# Revit family: BI-12FB
name_source: partatom
category: Устройства связи
units: mm (PartAtom-declared; Revit-internal decimal feet)

## family parameters
Всегда вертикально = Нет
На основе рабочей плоскости = Да
Общий = Да
При загрузке вырезать с полостями = Нет
Размер круглого соединителя = Использовать диаметр
Сохранять ориентацию аннотаций = Нет
Тип детали = Нормальный
Точка принадлежности помещению = Нет

## types (1)
- BI-12FB
    ADSK_URL документации изделия = https://wiki.bas-ip.com
    ADSK_URL страницы изделия = https://www.bas-ip.ru
    ADSK_Версия Revit = Revit 2020
    ADSK_Единица измерения = шт
    ADSK_Завод-изготовитель = BAS-IP
    ADSK_Классификация нагрузок = Вызывная панель
    ADSK_Количество фаз = 1
    ADSK_Коэффициент мощности = 0.9
    ADSK_Марка = BI-12FB
    ADSK_Наименование = ВЫЗЫВНАЯ ПАНЕЛЬ BI-12FB
    ADSK_Наименование краткое = BI-12FB
    ADSK_Напряжение = 12 В
    ADSK_Номинальная мощность = 7 Вт
    ADSK_Полная мощность = 7 В·А
    ADSK_Размер_Длина = 379 мм
    ADSK_Размер_Толщина = 49 мм
    ADSK_Размер_Ширина = 158 мм
    BIM library = https://bimlib.ru
    URL = https://www.bas-ip.ru
    Аутентификация = Отдельный пароль на настройки, WEB–интерфейс
    Выходное видео = HD (1920×1080), H.264 Main Profile
    Группа модели = Вызывная панель
    Дисплей = Нет
    Дополнительно = SIP P2P, Встроенное реле, датчик приближения, открытый API, поддержка ПО Link
    Изготовитель = BAS-IP
    Изображение типоразмера = <Нет>
    Интеграция со СКУД = Выход WIEGAND-26, 32, 34, 37, 40, 42, 56, 58, 64 бит
    Интерфейс = Мультиязычный WEB–интерфейс
    Камера = 1/3”
    Класс степени защиты = IP65
    Кнопки быстрого вызова = Кнопка вызова консьержа
    Количество мелодий вызова = Возможность установки пользовательской мелодии
    Контроль доступа = Мультиформатный считыватель с поддержкой технологии UKEY (EM-Marin, Mifare, BLE, NFC), 3D датчик распознавания лица
    Корпус = Металлический
    Материал корпуса = Материал серый
    Минимальная освещенность = 0,01 LuX
    Ночная подсветка = 6 светодиодов
    Описание = BAS-IP BI-12FB - Вызывные панели BI-02B, BI-04B, BI-06B, BI-08B, BI-12B доступны в золотом, серебряном и черном цветах. Они оснащены широкоугольной камерой и поддерживают мобильный доступ BAS-IP UKEY.
С помощью этих панелей можно совершать прямые звонки как на внутренние мониторы, так и на монитора консьержа. Устройство отлично вписывается в интерьер небольшого офиса или коттеджа
    Открытие замка = С монитора, по HTTP, по коду, по карте, из приложения UKEY, из приложения BAS-IP Intercom, по распознаванию лиц
    Отметка по умолчанию = 0 мм
    Питание = +12 В (+8% -4%) и PoE
    Поддерживаемые аудиокодеки = G.711u
    Потребление питания = 6,5 Вт, в режиме ожидания – 3,6 Вт
    Размер панели = 158х379х49 мм
    Размер под установку = 141х359х58 мм
    Разрешение камеры = 2.0 Мп
    Режим разговора = Двухсторонний
    Температурный режим = -40 ... +65 °С
    Тип клавиатуры = Механические кнопки с подсветкой
    Тип панели = Многокнопочная
    Тип установки = Врезная, накладная с BR-AA12
    Угол обзора = По горизонтали 90°, по вертикали 62°
    Цветовое решение = Серебро, Золото, Чёрный
